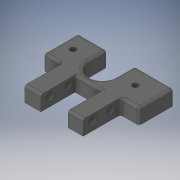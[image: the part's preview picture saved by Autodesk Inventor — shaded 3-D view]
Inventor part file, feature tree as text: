
AUTODESK INVENTOR PART (.ipt)
format: ipt  version: 2018 (Build 220112000, 112)  size: 436,224 bytes
history: native  units: mm
features: extrude x6, sketch x6, projected_geometry x3, fillet x1
ambient origin geometry x8: Origin, YZ Plane, XZ Plane, XY Plane, X Axis, Y Axis, Z Axis, Center Point
bodies: Volumenkörper1 (feature_tree)
feature tree (16):
  extrude  "Extrusion1"  Depth=58.0mm
  extrude  "Extrusion2"  Depth=12.0mm
  extrude  "Extrusion3"  Depth=27.5mm
  extrude  "Extrusion4"  Depth=10.0mm
  extrude  "Extrusion5"  Depth=10.0mm
  fillet  "Rundung2"  Radius=10.0mm
  extrude  "Extrusion6"  Depth=10.0mm
  sketch  "Skizze1"  dims[d0=77.0mm d1=58.0mm]
  sketch  "Skizze2"  dims[d2=12.0mm d3=0.0mm d4=28.0mm]
  sketch  "Skizze3"  dims[d5=27.0mm d6=27.5mm]
  projected_geometry  "Projizierte Kontur1"
  sketch  "Skizze4"  dims[d7=10.0mm d8=0.0mm d9=15.0mm]
  projected_geometry  "Projizierte Kontur2"
  sketch  "Skizze5"  dims[d10=15.0mm d11=22.0mm d12=10.0mm d13=0.0mm]
  projected_geometry  "Projizierte Kontur3"
  sketch  "Skizze6"  dims[d15=69.0mm d16=15.0mm d17=15.0mm d18=10.0mm d19=0.0mm d20=6.5mm d21=6.0mm d22=7.0mm d23=7.0mm d24=7.5mm d25=8.0mm d26=10.0mm d27=0.0mm d29=2.0mm d30=4.5mm d31=9.5mm d32=13.5mm d33=13.5mm d34=4.5mm d35=17.5mm d36=10.0mm d37=0.0mm d38=30.0mm]
